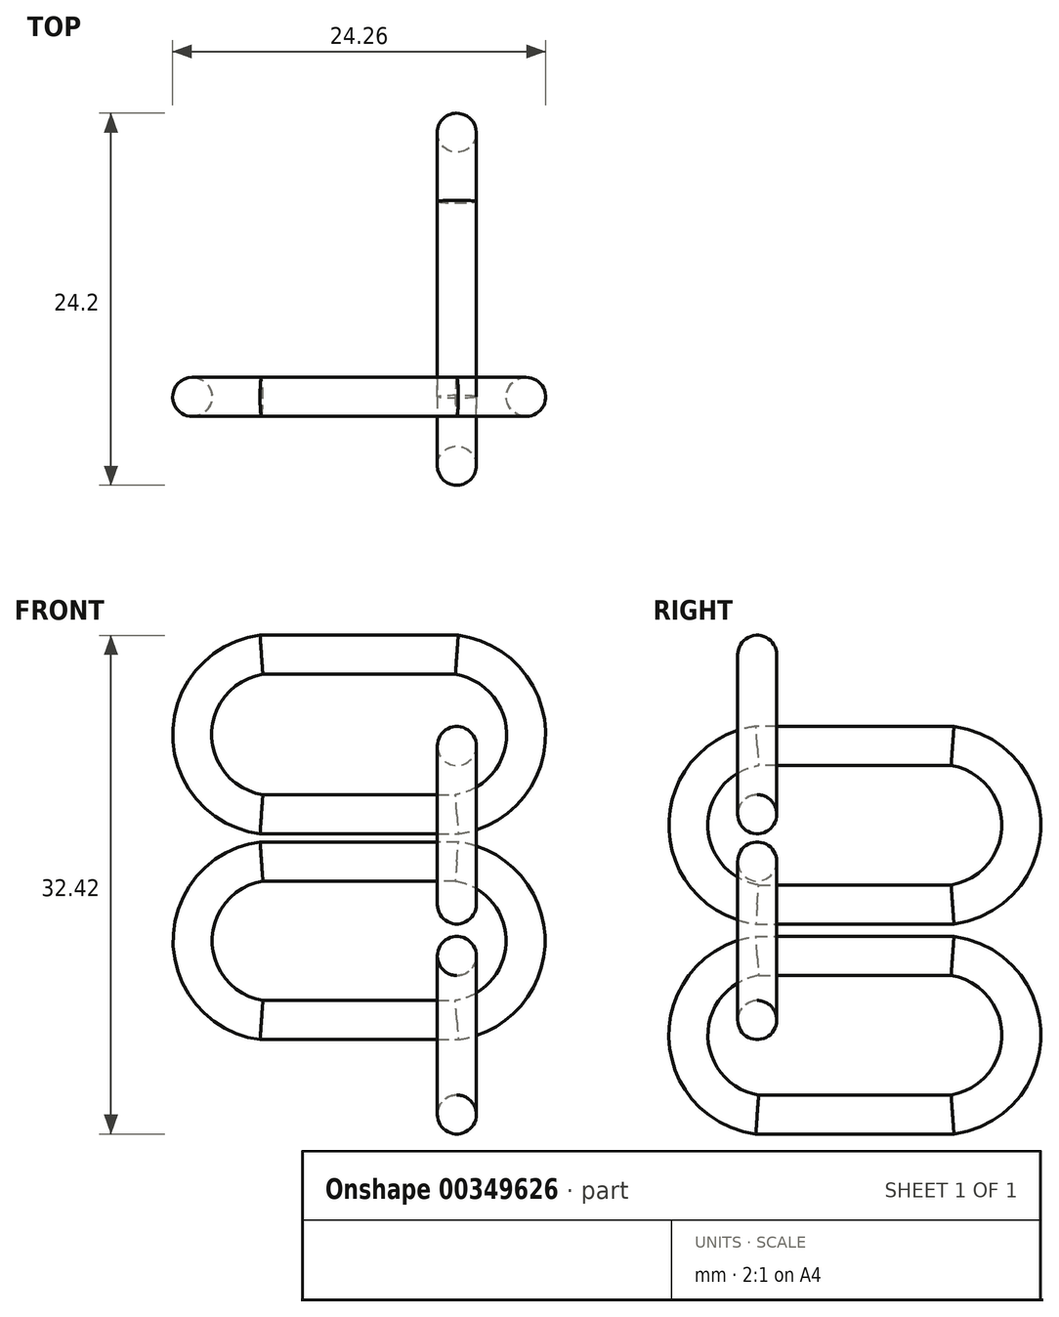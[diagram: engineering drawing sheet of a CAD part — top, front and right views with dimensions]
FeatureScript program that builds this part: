
annotation { "Feature Type Name" : "Feature", "Feature Type Description" : "" }
export const myFeature = defineFeature(function(context is Context, id is Id, definition is map)
    precondition{}
    {
        {
            var Q0;
            Q0=qCreatedBy(makeId("Front.planeOp"),FACE);
            var sketch = newSketch(context, id + "F0", { "sketchPlane" : qUnion([Q0])});
            skLineSegment(sketch, "E0", {"start": v(-12.7, 2.8) * mm, "end": v(0, 2.8) * mm});
            skLineSegment(sketch, "E1", {"start": v(-12.7, -7.51) * mm, "end": v(0, -7.51) * mm});
            skArc(sketch, "E2", {"start": v(0, -7.51) * mm, "mid": v(4.48, -2.36) * mm, "end": v(0, 2.8) * mm});
            skArc(sketch, "E3", {"start": v(-12.7, 2.8) * mm, "mid": v(-17.18, -2.36) * mm, "end": v(-12.7, -7.51) * mm});
            skSolve(sketch);
        }
        {
            var Q0;
            Q0=qCreatedBy(makeId("Front.planeOp"),FACE);
            var sketch = newSketch(context, id + "F1", { "sketchPlane" : qUnion([Q0])});
            skLineSegment(sketch, "E4", {"start": v(0, 5.9) * mm, "end": v(-12.7, 5.9) * mm});
            skLineSegment(sketch, "E5", {"start": v(0, 16.2) * mm, "end": v(-12.7, 16.2) * mm});
            skArc(sketch, "E6", {"start": v(-12.7, 16.2) * mm, "mid": v(-17.18, 11.05) * mm, "end": v(-12.7, 5.9) * mm});
            skArc(sketch, "E7", {"start": v(0, 5.9) * mm, "mid": v(4.48, 11.05) * mm, "end": v(0, 16.2) * mm});
            skSolve(sketch);
        }
        {
            var Q0;
            Q0=qCreatedBy(makeId("Right.planeOp"),FACE);
            var sketch = newSketch(context, id + "F2", { "sketchPlane" : qUnion([Q0])});
            skCircle(sketch, "E8", {"center": v(0, 2.8) * mm, "radius": 1.27 * mm});
            skCircle(sketch, "E9", {"center": v(0, 16.23) * mm, "radius": 1.27 * mm});
            skSolve(sketch);
        }
        {
            var Q0;
            Q0=makeQuery(id+"F2.imprint","IMPRINT",FACE,{"disambiguationData":[TD([[makeQuery(id+"F2.imprint","IMPRINT",EDGE,{"derivedFrom":sQuery(id+"F2.wireOp",EDGE,"E8")}),1.0]])]});
            var Q1;
            Q1=sQuery(id+"F0.wireOp",EDGE,"E0");
            var Q2;
            Q2=sQuery(id+"F0.wireOp",EDGE,"E3");
            var Q3;
            Q3=sQuery(id+"F0.wireOp",EDGE,"E1");
            var Q4;
            Q4=sQuery(id+"F0.wireOp",EDGE,"E2");
            sweep(context, id + "F3", {"profiles" : qUnion([Q0]), "path" : qUnion([Q1, Q2, Q3, Q4])});
        }
        {
            var Q0;
            Q0=qCreatedBy(makeId("Right.planeOp"),FACE);
            var sketch = newSketch(context, id + "F4", { "sketchPlane" : qUnion([Q0])});
            skLineSegment(sketch, "E10", {"start": v(0, 10.3) * mm, "end": v(12.7, 10.3) * mm});
            skLineSegment(sketch, "E11", {"start": v(0, 0) * mm, "end": v(12.7, 0) * mm});
            skArc(sketch, "E12", {"start": v(12.7, 0) * mm, "mid": v(17.18, 5.15) * mm, "end": v(12.7, 10.3) * mm});
            skArc(sketch, "E13", {"start": v(0, 10.3) * mm, "mid": v(-4.48, 5.15) * mm, "end": v(0, 0) * mm});
            skSolve(sketch);
        }
        {
            var Q0;
            Q0=qCreatedBy(makeId("Front.planeOp"),FACE);
            var sketch = newSketch(context, id + "F5", { "sketchPlane" : qUnion([Q0])});
            skCircle(sketch, "E14", {"center": v(0, 0) * mm, "radius": 1.27 * mm});
            skSolve(sketch);
        }
        {
            var Q0;
            Q0=makeQuery(id+"F5.imprint","IMPRINT",FACE,{"disambiguationData":[TD([[makeQuery(id+"F5.imprint","IMPRINT",EDGE,{"derivedFrom":sQuery(id+"F5.wireOp",EDGE,"E14")}),1.0]])]});
            var Q1;
            Q1=sQuery(id+"F4.wireOp",EDGE,"E11");
            var Q2;
            Q2=sQuery(id+"F4.wireOp",EDGE,"E12");
            var Q3;
            Q3=sQuery(id+"F4.wireOp",EDGE,"E10");
            var Q4;
            Q4=sQuery(id+"F4.wireOp",EDGE,"E13");
            sweep(context, id + "F6", {"profiles" : qUnion([Q0]), "path" : qUnion([Q1, Q2, Q3, Q4])});
        }
        {
            var Q0;
            Q0=qCreatedBy(makeId("Right.planeOp"),FACE);
            var sketch = newSketch(context, id + "F7", { "sketchPlane" : qUnion([Q0])});
            skLineSegment(sketch, "E15", {"start": v(0, -3.35) * mm, "end": v(12.7, -3.35) * mm});
            skLineSegment(sketch, "E16", {"start": v(0, -13.65) * mm, "end": v(12.7, -13.65) * mm});
            skArc(sketch, "E17", {"start": v(12.7, -13.65) * mm, "mid": v(17.18, -8.5) * mm, "end": v(12.7, -3.35) * mm});
            skArc(sketch, "E18", {"start": v(0, -3.35) * mm, "mid": v(-4.48, -8.5) * mm, "end": v(0, -13.65) * mm});
            skSolve(sketch);
        }
        {
            var Q0;
            Q0=qCreatedBy(makeId("Front.planeOp"),FACE);
            var sketch = newSketch(context, id + "F8", { "sketchPlane" : qUnion([Q0])});
            skCircle(sketch, "E19", {"center": v(0, -3.35) * mm, "radius": 1.27 * mm});
            skSolve(sketch);
        }
        {
            var Q0;
            Q0=makeQuery(id+"F8.imprint","IMPRINT",FACE,{"disambiguationData":[TD([[makeQuery(id+"F8.imprint","IMPRINT",EDGE,{"derivedFrom":sQuery(id+"F8.wireOp",EDGE,"E19")}),1.0]])]});
            var Q1;
            Q1=sQuery(id+"F7.wireOp",EDGE,"E15");
            var Q2;
            Q2=sQuery(id+"F7.wireOp",EDGE,"E17");
            var Q3;
            Q3=sQuery(id+"F7.wireOp",EDGE,"E16");
            var Q4;
            Q4=sQuery(id+"F7.wireOp",EDGE,"E18");
            sweep(context, id + "F9", {"profiles" : qUnion([Q0]), "path" : qUnion([Q1, Q2, Q3, Q4])});
        }
        {
            var Q0;
            Q0=makeQuery(id+"F2.imprint","IMPRINT",FACE,{"disambiguationData":[TD([[makeQuery(id+"F2.imprint","IMPRINT",EDGE,{"derivedFrom":sQuery(id+"F2.wireOp",EDGE,"E9")}),1.0]])]});
            var Q1;
            Q1=sQuery(id+"F1.wireOp",EDGE,"E5");
            var Q2;
            Q2=sQuery(id+"F1.wireOp",EDGE,"E6");
            var Q3;
            Q3=sQuery(id+"F1.wireOp",EDGE,"E4");
            var Q4;
            Q4=sQuery(id+"F1.wireOp",EDGE,"E7");
            sweep(context, id + "F10", {"profiles" : qUnion([Q0]), "path" : qUnion([Q1, Q2, Q3, Q4])});
        }
    });
